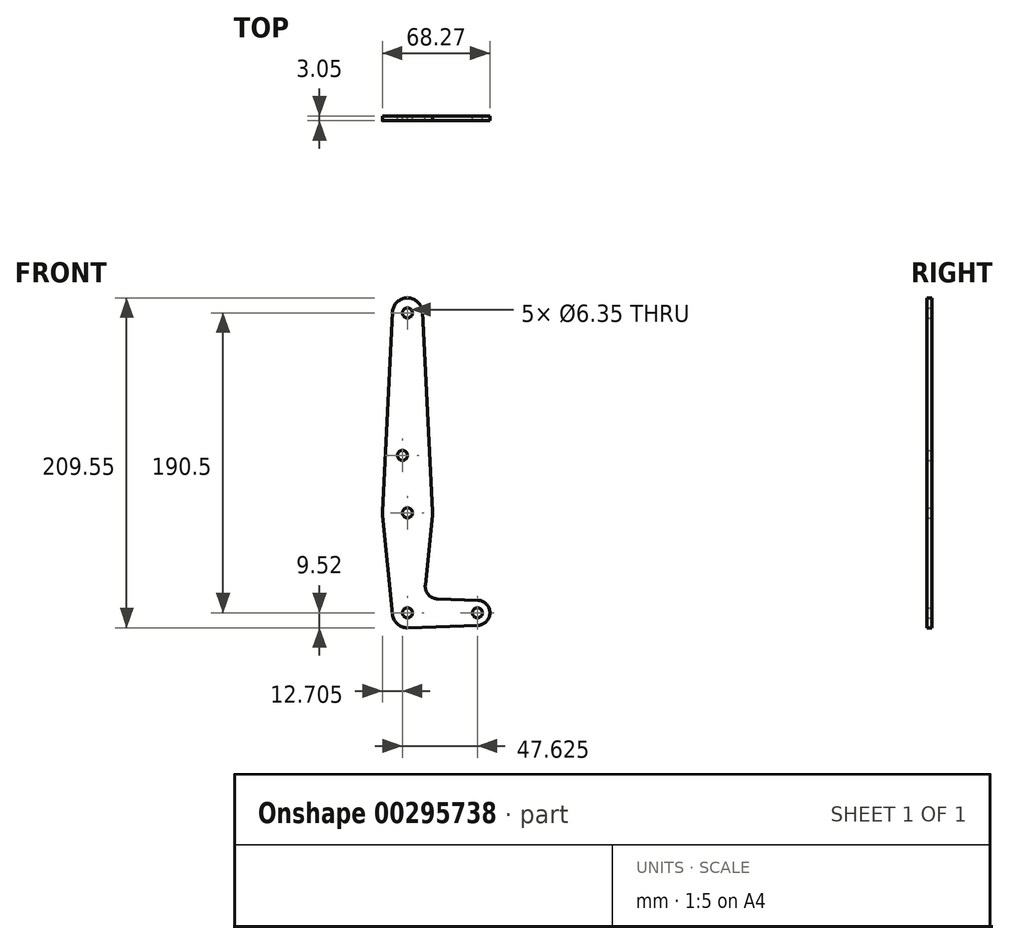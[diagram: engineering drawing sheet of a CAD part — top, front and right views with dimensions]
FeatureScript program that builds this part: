
annotation { "Feature Type Name" : "Feature", "Feature Type Description" : "" }
export const myFeature = defineFeature(function(context is Context, id is Id, definition is map)
    precondition{}
    {
        {
            var Q0;
            Q0=qCreatedBy(makeId("Front.planeOp"),FACE);
            var sketch = newSketch(context, id + "F0", { "sketchPlane" : qUnion([Q0])});
            skLineSegment(sketch, "E0", {"start": v(0, 0) * mm, "end": v(0, 63.5) * mm, "construction": true});
            skLineSegment(sketch, "E1", {"start": v(0, 190.5) * mm, "end": v(0, 63.5) * mm, "construction": true});
            skLineSegment(sketch, "E2", {"start": v(0, 0) * mm, "end": v(44.45, 0) * mm, "construction": true});
            skCircle(sketch, "E3", {"center": v(0, 190.5) * mm, "radius": 9.53 * mm});
            skCircle(sketch, "E4", {"center": v(0, 63.5) * mm, "radius": 15.88 * mm});
            skCircle(sketch, "E5", {"center": v(0, 0) * mm, "radius": 9.53 * mm});
            skCircle(sketch, "E6", {"center": v(44.45, 0) * mm, "radius": 7.94 * mm});
            skLineSegment(sketch, "E7", {"start": v(-9.51, 190.98) * mm, "end": v(-15.86, 64.3) * mm});
            skLineSegment(sketch, "E8", {"start": v(-15.8, 61.91) * mm, "end": v(-9.48, -0.95) * mm});
            skLineSegment(sketch, "E9", {"start": v(9.51, 190.98) * mm, "end": v(15.86, 64.3) * mm});
            skLineSegment(sketch, "E10", {"start": v(15.8, 61.91) * mm, "end": v(11.34, 17.6) * mm});
            skLineSegment(sketch, "E11", {"start": v(18.97, 8.85) * mm, "end": v(44.73, 7.93) * mm});
            skLineSegment(sketch, "E12", {"start": v(0.34, -9.52) * mm, "end": v(44.73, -7.93) * mm});
            skCircle(sketch, "E13", {"center": v(0, 190.5) * mm, "radius": 3.18 * mm});
            skCircle(sketch, "E14", {"center": v(0, 63.5) * mm, "radius": 3.18 * mm});
            skCircle(sketch, "E15", {"center": v(0, 0) * mm, "radius": 3.18 * mm});
            skCircle(sketch, "E16", {"center": v(44.45, 0) * mm, "radius": 3.18 * mm});
            skCircle(sketch, "E17", {"center": v(-3.17, 100.03) * mm, "radius": 3.18 * mm});
            skArc(sketch, "E18.filletArc", {"start": v(11.34, 17.6) * mm, "mid": v(13.26, 11.57) * mm, "end": v(18.97, 8.85) * mm});
            skSolve(sketch);
        }
        {
            var Q0;
            Q0 = qSketchRegion(id + "F0", true);
            extrude(context, id + "F1", {"entities" : qUnion([Q0]), "depth" : 3.05 * mm});
        }
    });
